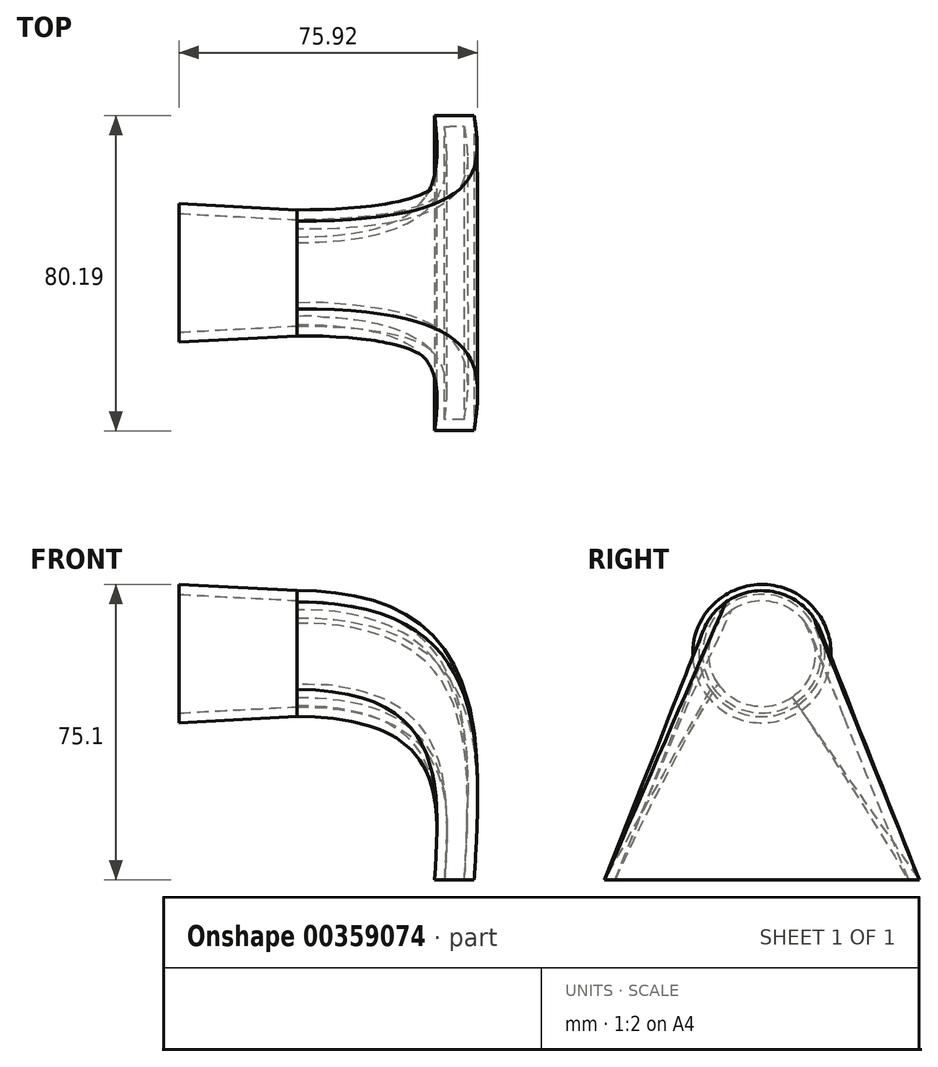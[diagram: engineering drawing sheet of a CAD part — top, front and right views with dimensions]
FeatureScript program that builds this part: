
annotation { "Feature Type Name" : "Feature", "Feature Type Description" : "" }
export const myFeature = defineFeature(function(context is Context, id is Id, definition is map)
    precondition{}
    {
        {
            var Q0;
            Q0=qCreatedBy(makeId("Right.planeOp"),FACE);
            var sketch = newSketch(context, id + "F0", { "sketchPlane" : qUnion([Q0])});
            skCircle(sketch, "E0", {"center": v(0, 57.51) * mm, "radius": 16 * mm});
            skSolve(sketch);
        }
        {
            var Q0;
            Q0=qCreatedBy(makeId("Top.planeOp"),FACE);
            var sketch = newSketch(context, id + "F1", { "sketchPlane" : qUnion([Q0])});
            skLineSegment(sketch, "E1.bottom", {"start": v(35, 40) * mm, "end": v(45, 40) * mm});
            skLineSegment(sketch, "E1.top", {"start": v(35, -40) * mm, "end": v(45, -40) * mm});
            skLineSegment(sketch, "E1.left", {"start": v(35, 40) * mm, "end": v(35, -40) * mm});
            skLineSegment(sketch, "E1.right", {"start": v(45, 40) * mm, "end": v(45, -40) * mm});
            skPoint(sketch, "E1.middle", {"position": v(40, 0) * mm});
            skSolve(sketch);
        }
        {
            var Q0;
            Q0=makeQuery(id+"F0.imprint","IMPRINT",FACE,{"disambiguationData":[TD([[makeQuery(id+"F0.imprint","IMPRINT",EDGE,{"derivedFrom":sQuery(id+"F0.wireOp",EDGE,"E0")}),1.0]])]});
            var Q1;
            Q1=makeQuery(id+"F1.imprint","IMPRINT",FACE,{"disambiguationData":[TD([[makeQuery(id+"F1.imprint","IMPRINT",EDGE,{"derivedFrom":sQuery(id+"F1.wireOp",EDGE,"E1.bottom")}),-1.0]])]});
            loft(context, id + "F2", {"startCondition" : LoftEndDerivativeType.NORMAL_TO_PROFILE, "startMagnitude" : 3, "sheetProfilesArray" : [{ "sheetProfileEntities" : qUnion([Q0]) }, { "sheetProfileEntities" : qUnion([Q1]) }]});
        }
        {
            var Q0;
            Q0=makeQuery(id+"F2.opLoft","CAP_FACE",FACE,{"disambiguationData":[OSD([makeQuery(id+"F0.imprint","IMPRINT",FACE,{"disambiguationData":[TD([[makeQuery(id+"F0.imprint","IMPRINT",EDGE,{"derivedFrom":sQuery(id+"F0.wireOp",EDGE,"E0")}),1.0]])]})])],"isStart":true});
            extrude(context, id + "F3", {"entities" : qUnion([Q0]), "operationType" : NewBodyOperationType.ADD, "depth" : 30 * mm, "hasDraft" : true, "draftAngle" : 3 * degree});
        }
        {
            var Q0;
            Q0=makeQuery(id+"F3.opExtrude","CAP_FACE",FACE,{"disambiguationData":[OSD([makeQuery(id+"F0.imprint","IMPRINT",FACE,{"disambiguationData":[TD([[makeQuery(id+"F0.imprint","IMPRINT",EDGE,{"derivedFrom":sQuery(id+"F0.wireOp",EDGE,"E0")}),1.0]])]})])],"isStart":false});
            var Q1;
            Q1=makeQuery(id+"F2.opLoft","CAP_FACE",FACE,{"disambiguationData":[OSD([makeQuery(id+"F1.imprint","IMPRINT",FACE,{"disambiguationData":[TD([[makeQuery(id+"F1.imprint","IMPRINT",EDGE,{"derivedFrom":sQuery(id+"F1.wireOp",EDGE,"E1.bottom")}),-1.0]])]})])],"isStart":true});
            shell(context, id + "F4", {"entities" : qUnion([Q0, Q1]), "thickness" : 2.5 * mm});
        }
    });
